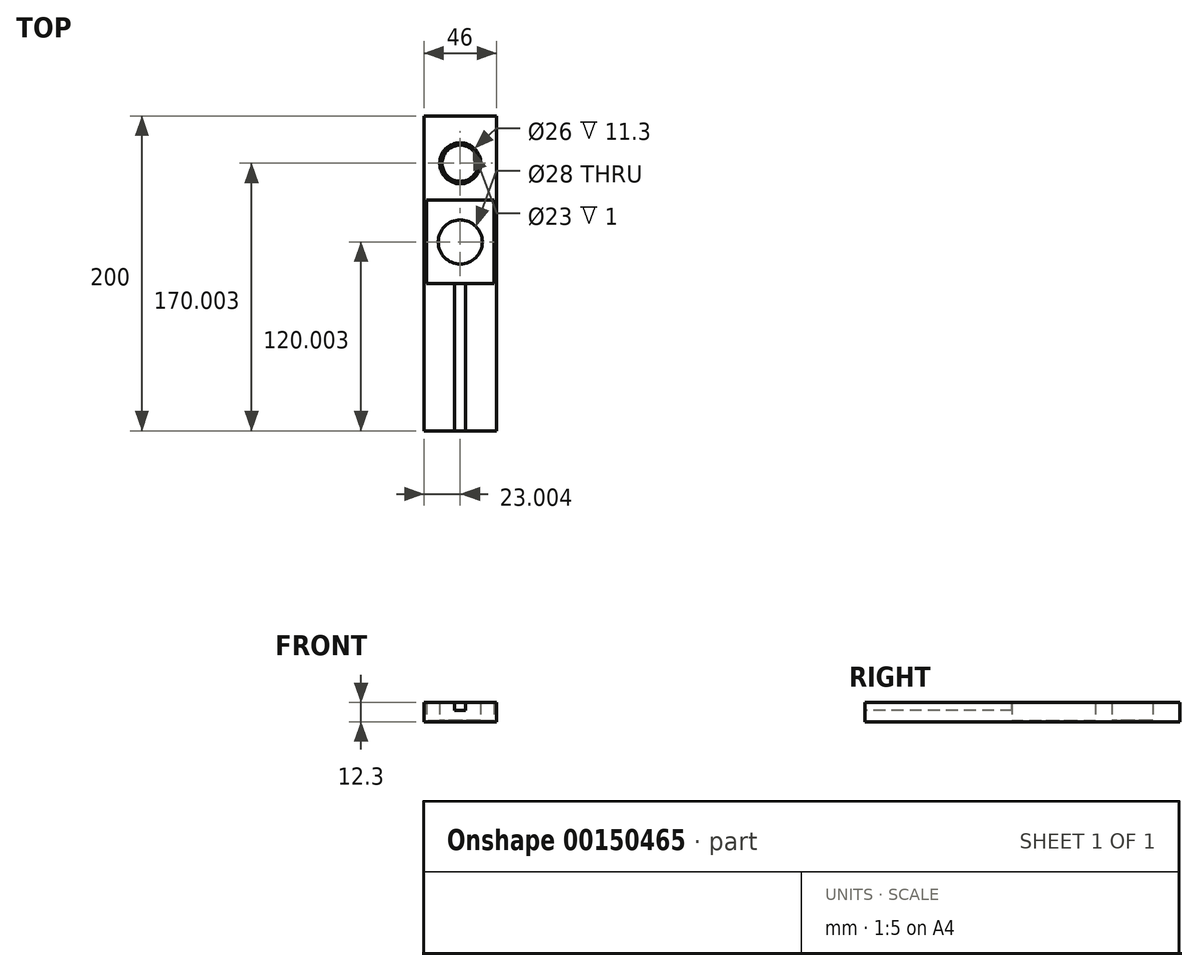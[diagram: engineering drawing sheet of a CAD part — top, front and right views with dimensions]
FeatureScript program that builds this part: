
annotation { "Feature Type Name" : "Feature", "Feature Type Description" : "" }
export const myFeature = defineFeature(function(context is Context, id is Id, definition is map)
    precondition{}
    {
        {
            var Q0;
            Q0=qCreatedBy(makeId("Top.planeOp"),FACE);
            var sketch = newSketch(context, id + "F0", { "sketchPlane" : qUnion([Q0])});
            skLineSegment(sketch, "E0.bottom", {"start": v(23.97, -95.42) * mm, "end": v(-22.03, -95.42) * mm});
            skLineSegment(sketch, "E0.top", {"start": v(23.97, 104.58) * mm, "end": v(-22.03, 104.58) * mm});
            skLineSegment(sketch, "E0.left", {"start": v(23.97, -95.42) * mm, "end": v(23.97, 104.58) * mm});
            skLineSegment(sketch, "E0.right", {"start": v(-22.03, -95.42) * mm, "end": v(-22.03, 104.58) * mm});
            skCircle(sketch, "E1", {"center": v(0.97, 24.58) * mm, "radius": 14 * mm});
            skLineSegment(sketch, "E2.bottom", {"start": v(22.47, 51.08) * mm, "end": v(-20.53, 51.08) * mm});
            skLineSegment(sketch, "E2.top", {"start": v(22.47, -1.92) * mm, "end": v(-20.53, -1.92) * mm});
            skLineSegment(sketch, "E2.left", {"start": v(22.47, 51.08) * mm, "end": v(22.47, -1.92) * mm});
            skLineSegment(sketch, "E2.right", {"start": v(-20.53, 51.08) * mm, "end": v(-20.53, -1.92) * mm});
            skCircle(sketch, "E3", {"center": v(0.97, 74.58) * mm, "radius": 13 * mm});
            skCircle(sketch, "E4", {"center": v(0.97, 74.58) * mm, "radius": 11.5 * mm});
            skSolve(sketch);
        }
        {
            var Q0;
            Q0=makeQuery(id+"F0.imprint","IMPRINT",FACE,{"disambiguationData":[TD([[makeQuery(id+"F0.imprint","IMPRINT",EDGE,{"derivedFrom":sQuery(id+"F0.wireOp",EDGE,"E0.bottom")}),-1.0]])]});
            extrude(context, id + "F1", {"entities" : qUnion([Q0]), "depth" : 11.8 * mm});
        }
        {
            var Q0;
            Q0=makeQuery(id+"F0.imprint","IMPRINT",FACE,{"disambiguationData":[TD([[makeQuery(id+"F0.imprint","IMPRINT",EDGE,{"derivedFrom":sQuery(id+"F0.wireOp",EDGE,"E1")}),-1.0]])]});
            var Q1;
            Q1=makeQuery(id+"F1.opExtrude","CAP_FACE",FACE,{"disambiguationData":[OSD([sQuery(id+"F0.wireOp",EDGE,"E0.bottom"),sQuery(id+"F0.wireOp",EDGE,"E0.top"),sQuery(id+"F0.wireOp",EDGE,"E0.left"),sQuery(id+"F0.wireOp",EDGE,"E0.right"),sQuery(id+"F0.wireOp",EDGE,"E2.bottom"),sQuery(id+"F0.wireOp",EDGE,"E2.top"),sQuery(id+"F0.wireOp",EDGE,"E2.left"),sQuery(id+"F0.wireOp",EDGE,"E2.right")])],"isStart":false});
            extrude(context, id + "F2", {"entities" : qUnion([Q0, Q1]), "operationType" : NewBodyOperationType.ADD, "depth" : 0.5 * mm});
        }
        {
            var Q0;
            Q0=makeQuery(id+"F2.opExtrude","CAP_FACE",FACE,{"disambiguationData":[OSD([sQuery(id+"F0.wireOp",EDGE,"E0.bottom"),sQuery(id+"F0.wireOp",EDGE,"E0.top"),sQuery(id+"F0.wireOp",EDGE,"E0.left"),sQuery(id+"F0.wireOp",EDGE,"E0.right"),sQuery(id+"F0.wireOp",EDGE,"E2.bottom"),sQuery(id+"F0.wireOp",EDGE,"E2.top"),sQuery(id+"F0.wireOp",EDGE,"E2.left"),sQuery(id+"F0.wireOp",EDGE,"E2.right")])],"isStart":false});
            var sketch = newSketch(context, id + "F3", { "sketchPlane" : qUnion([Q0])});
            skLineSegment(sketch, "E5.bottom", {"start": v(-2.53, -1.92) * mm, "end": v(4.47, -1.92) * mm});
            skLineSegment(sketch, "E5.top", {"start": v(-2.53, -95.42) * mm, "end": v(4.47, -95.42) * mm});
            skLineSegment(sketch, "E5.left", {"start": v(-2.53, -1.92) * mm, "end": v(-2.53, -95.42) * mm});
            skLineSegment(sketch, "E5.right", {"start": v(4.47, -1.92) * mm, "end": v(4.47, -95.42) * mm});
            skSolve(sketch);
        }
        {
            var Q0;
            Q0=makeQuery(id+"F3.imprint","IMPRINT",FACE,{"disambiguationData":[TD([[makeQuery(id+"F3.imprint","IMPRINT",EDGE,{"derivedFrom":sQuery(id+"F3.wireOp",EDGE,"E5.bottom")}),1.0]])]});
            extrude(context, id + "F4", {"entities" : qUnion([Q0]), "operationType" : NewBodyOperationType.REMOVE, "oppositeDirection" : true, "depth" : 5 * mm});
        }
        {
            var Q0;
            Q0=makeQuery(id+"F0.imprint","IMPRINT",FACE,{"disambiguationData":[TD([[makeQuery(id+"F0.imprint","IMPRINT",EDGE,{"derivedFrom":sQuery(id+"F0.wireOp",EDGE,"E3")}),1.0]])]});
            extrude(context, id + "F5", {"entities" : qUnion([Q0]), "operationType" : NewBodyOperationType.ADD, "depth" : 1 * mm});
        }
    });
